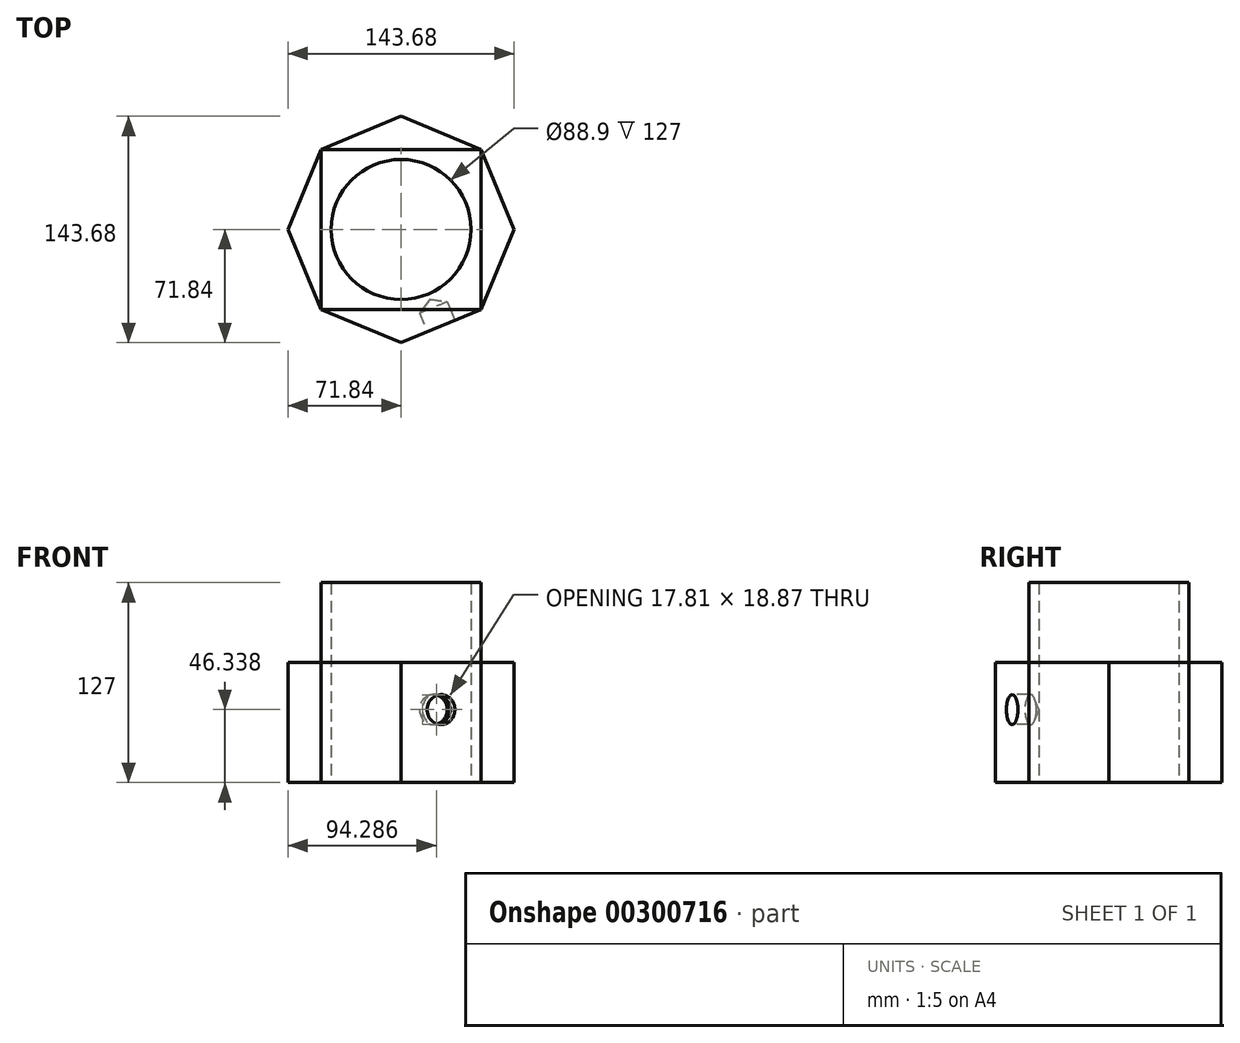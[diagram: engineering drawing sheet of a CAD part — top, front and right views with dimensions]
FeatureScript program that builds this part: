
annotation { "Feature Type Name" : "Feature", "Feature Type Description" : "" }
export const myFeature = defineFeature(function(context is Context, id is Id, definition is map)
    precondition{}
    {
        {
            var Q0;
            Q0=qCreatedBy(makeId("Top.planeOp"),FACE);
            var sketch = newSketch(context, id + "F0", { "sketchPlane" : qUnion([Q0])});
            skLineSegment(sketch, "E0.bottom", {"start": v(50.8, -50.8) * mm, "end": v(-50.8, -50.8) * mm});
            skLineSegment(sketch, "E0.top", {"start": v(50.8, 50.8) * mm, "end": v(-50.8, 50.8) * mm});
            skLineSegment(sketch, "E0.left", {"start": v(50.8, -50.8) * mm, "end": v(50.8, 50.8) * mm});
            skLineSegment(sketch, "E0.right", {"start": v(-50.8, -50.8) * mm, "end": v(-50.8, 50.8) * mm});
            skPoint(sketch, "E0.middle", {"position": v(0, 0) * mm});
            skCircle(sketch, "E1.cCircle", {"center": v(0, 0) * mm, "radius": 71.84 * mm, "construction": true});
            skLineSegment(sketch, "E1.0", {"start": v(50.8, 50.8) * mm, "end": v(71.84, 0) * mm});
            skLineSegment(sketch, "E1.1", {"start": v(71.84, 0) * mm, "end": v(50.8, -50.8) * mm});
            skLineSegment(sketch, "E1.2", {"start": v(50.8, -50.8) * mm, "end": v(0, -71.84) * mm});
            skLineSegment(sketch, "E1.3", {"start": v(0, -71.84) * mm, "end": v(-50.8, -50.8) * mm});
            skLineSegment(sketch, "E1.4", {"start": v(-50.8, -50.8) * mm, "end": v(-71.84, 0) * mm});
            skLineSegment(sketch, "E1.5", {"start": v(-71.84, 0) * mm, "end": v(-50.8, 50.8) * mm});
            skLineSegment(sketch, "E1.6", {"start": v(-50.8, 50.8) * mm, "end": v(0, 71.84) * mm});
            skLineSegment(sketch, "E1.7", {"start": v(0, 71.84) * mm, "end": v(50.8, 50.8) * mm});
            skSolve(sketch);
        }
        {
            var Q0;
            Q0=makeQuery(id+"F0.imprint","IMPRINT",FACE,{"disambiguationData":[TD([[makeQuery(id+"F0.imprint","IMPRINT",EDGE,{"derivedFrom":sQuery(id+"F0.wireOp",EDGE,"E0.bottom")}),1.0]])]});
            var Q1;
            Q1=makeQuery(id+"F0.imprint","IMPRINT",FACE,{"disambiguationData":[TD([[makeQuery(id+"F0.imprint","IMPRINT",EDGE,{"derivedFrom":sQuery(id+"F0.wireOp",EDGE,"E0.top")}),-1.0]])]});
            var Q2;
            Q2=makeQuery(id+"F0.imprint","IMPRINT",FACE,{"disambiguationData":[TD([[makeQuery(id+"F0.imprint","IMPRINT",EDGE,{"derivedFrom":sQuery(id+"F0.wireOp",EDGE,"E0.left")}),-1.0]])]});
            var Q3;
            Q3=makeQuery(id+"F0.imprint","IMPRINT",FACE,{"disambiguationData":[TD([[makeQuery(id+"F0.imprint","IMPRINT",EDGE,{"derivedFrom":sQuery(id+"F0.wireOp",EDGE,"E0.right")}),1.0]])]});
            extrude(context, id + "F1", {"entities" : qUnion([Q0, Q1, Q2, Q3]), "depth" : 76.2 * mm});
        }
        {
            var Q0;
            Q0=makeQuery(id+"F0.imprint","IMPRINT",FACE,{"disambiguationData":[TD([[makeQuery(id+"F0.imprint","IMPRINT",EDGE,{"derivedFrom":sQuery(id+"F0.wireOp",EDGE,"E0.bottom")}),-1.0]])]});
            extrude(context, id + "F2", {"entities" : qUnion([Q0]), "depth" : 127 * mm});
        }
        {
            var Q0;
            Q0=sQuery(id+"F0.wireOp",VERTEX,"E0.middle");
            var Q1;
            Q1=makeQuery(id+"F2.opExtrude","SWEPT_BODY",BODY,{"disambiguationData":[OSD([sQuery(id+"F0.wireOp",EDGE,"E0.bottom"),sQuery(id+"F0.wireOp",EDGE,"E0.top"),sQuery(id+"F0.wireOp",EDGE,"E0.left"),sQuery(id+"F0.wireOp",EDGE,"E0.right")])]});
            hole(context, id + "F3", {"style" : HoleStyle.SIMPLE, "endStyle" : HoleEndStyle.THROUGH, "oppositeDirection" : true, "holeDiameter" : 88.9 * mm, "tappedDepth" : 12.7 * mm, "tapClearance" : 3, "locations" : qUnion([Q0]), "scope" : qUnion([Q1])});
        }
        {
            var Q0;
            Q0=makeQuery(id+"F1.opExtrude","SWEPT_FACE",FACE,{"disambiguationData":[OSD([sQuery(id+"F0.wireOp",EDGE,"E1.2")])]});
            var sketch = newSketch(context, id + "F4", { "sketchPlane" : qUnion([Q0])});
            skPoint(sketch, "E2", {"position": v(0, 46.34) * mm});
            skSolve(sketch);
        }
        {
            var Q0;
            Q0=sQuery(id+"F4.wireOp",VERTEX,"E2");
            var Q1;
            Q1=makeQuery(id+"F2.opExtrude","SWEPT_BODY",BODY,{"disambiguationData":[OSD([sQuery(id+"F0.wireOp",EDGE,"E0.bottom"),sQuery(id+"F0.wireOp",EDGE,"E0.top"),sQuery(id+"F0.wireOp",EDGE,"E0.left"),sQuery(id+"F0.wireOp",EDGE,"E0.right")])]});
            var Q2;
            Q2=makeQuery(id+"F1.opExtrude","SWEPT_BODY",BODY,{"disambiguationData":[OSD([sQuery(id+"F0.wireOp",EDGE,"E0.bottom"),sQuery(id+"F0.wireOp",EDGE,"E1.2"),sQuery(id+"F0.wireOp",EDGE,"E1.3")])]});
            hole(context, id + "F5", {"style" : HoleStyle.SIMPLE, "endStyle" : HoleEndStyle.BLIND, "holeDiameter" : 19.05 * mm, "holeDepth" : 12.7 * mm, "tappedDepth" : 12.7 * mm, "tapClearance" : 3, "locations" : qUnion([Q0]), "scope" : qUnion([Q1, Q2])});
        }
    });
